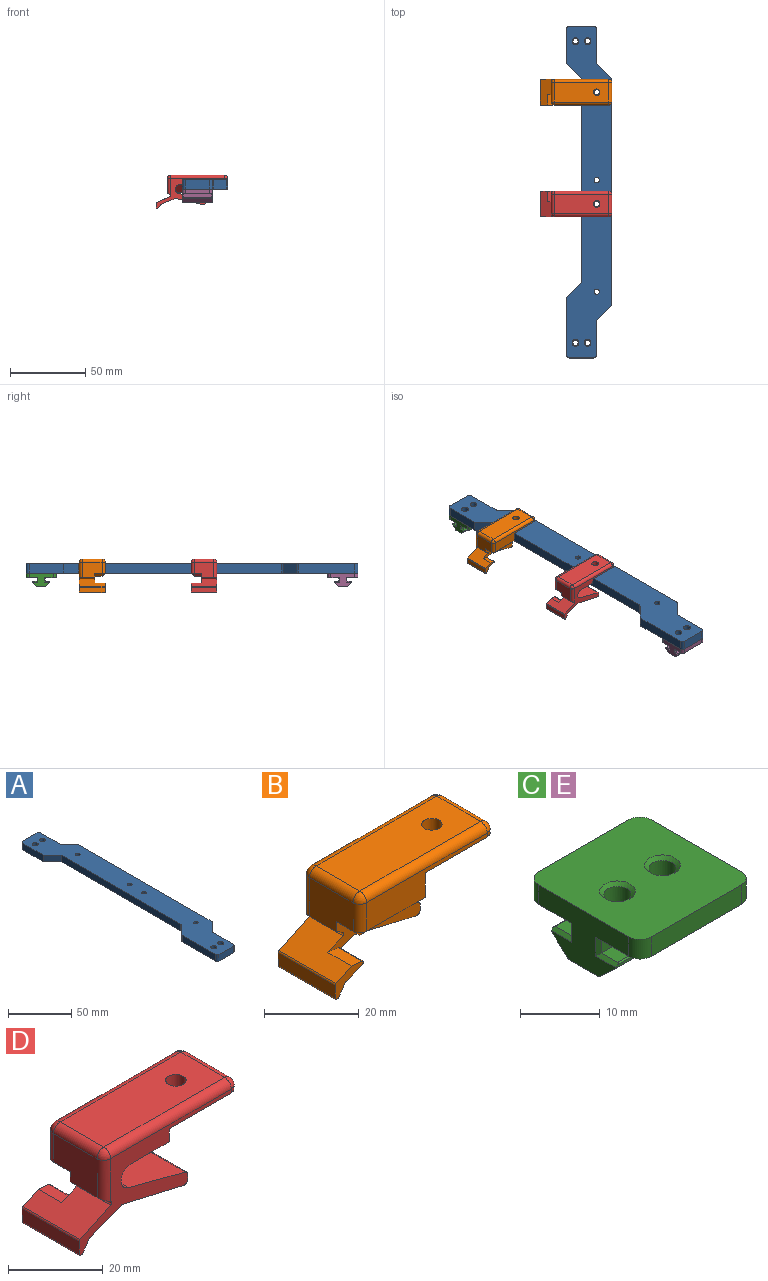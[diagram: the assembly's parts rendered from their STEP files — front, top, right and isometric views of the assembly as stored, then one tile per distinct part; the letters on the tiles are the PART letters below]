
ASSEMBLY  parts=5 mates=4
PART A: 32 faces, bbox 30x220x6.4 mm
  f0: plane 22.9x6.35mm, normal (-1,0,0), area 145.4mm2, adj f8,f9,f20,f31
  f1: plane 16x6.35mm, normal (0,-1,0), area 101.6mm2, adj f8,f9,f16,f17
  f2: plane 22.17x6.35mm, normal (1,0,0), area 140.8mm2, adj f8,f9,f16,f21
  f3: plane 148.34x6.35mm, normal (1,0,0), area 942mm2, adj f8,f9,f13,f14
  f4: plane 22.17x6.35mm, normal (1,0,0), area 140.8mm2, adj f8,f9,f18,f19
  f5: plane 16x6.35mm, normal (0,1,0), area 101.6mm2, adj f8,f9,f19,f20
  f6: plane 134.27x6.35mm, normal (-1,0,0), area 852.6mm2, adj f8,f9,f15,f31
  f7: plane 37.17x6.35mm, normal (-1,0,0), area 236mm2, adj f8,f9,f17,f22
  f8: plane 220x30mm, normal (0,0,1), area 4443.5mm2, adj f0,f1,f2,f3,f4,f5,f6,f7
  f9: plane 220x30mm, normal (0,0,-1), area 4443.5mm2, adj f0,f1,f2,f3,f4,f5,f6,f7
  f10: plane 8.83x8.83mm, normal (-0.71,0.71,0), area 79.3mm2, adj f8,f9,f15,f22
  f11: plane 8.83x8.83mm, normal (0.71,-0.71,0), area 79.3mm2, adj f8,f9,f13,f21
  f12: plane 8.83x8.83mm, normal (0.71,0.71,0), area 79.3mm2, adj f8,f9,f14,f18
  f13: cylinder r=2mm len=6.35mm, axis (0,0,1), area 10mm2, adj f3,f8,f9,f11
  f14: cylinder r=2mm len=6.35mm, axis (0,0,1), area 10mm2, adj f3,f8,f9,f12
  f15: cylinder r=2mm len=6.35mm, axis (0,0,1), area 10mm2, adj f6,f8,f9,f10
  f16: cylinder r=2mm len=6.35mm, axis (0,0,1), area 19.9mm2, adj f1,f2,f8,f9
  f17: cylinder r=2mm len=6.35mm, axis (0,0,-1), area 19.9mm2, adj f1,f7,f8,f9
  f18: cylinder r=2mm len=6.35mm, axis (0,0,1), area 10mm2, adj f4,f8,f9,f12
  f19: cylinder r=2mm len=6.35mm, axis (0,0,-1), area 19.9mm2, adj f4,f5,f8,f9
  f20: cylinder r=2mm len=6.35mm, axis (0,0,1), area 19.9mm2, adj f0,f5,f8,f9
  f21: cylinder r=2mm len=6.35mm, axis (0,0,-1), area 10mm2, adj f2,f8,f9,f11
  f22: cylinder r=2mm len=6.35mm, axis (0,0,1), area 10mm2, adj f7,f8,f9,f10
  f23: cylinder r=2.25mm len=6.35mm, axis (0,0,1), area 89.8mm2, adj f8,f9
  f24: cylinder r=2.25mm len=6.35mm, axis (0,0,1), area 89.8mm2, adj f8,f9
  f25: cylinder r=2.25mm len=6.35mm, axis (0,0,1), area 89.8mm2, adj f8,f9
  f26: cylinder r=2.25mm len=6.35mm, axis (0,0,1), area 89.8mm2, adj f8,f9
  f27: cylinder r=1.75mm len=6.35mm, axis (0,0,1), area 69.8mm2, adj f8,f9
  f28: cylinder r=1.75mm len=6.35mm, axis (0,0,1), area 69.8mm2, adj f8,f9
  f29: cylinder r=1.75mm len=6.35mm, axis (0,0,1), area 69.8mm2, adj f8,f9
  f30: cylinder r=1.75mm len=6.35mm, axis (0,0,1), area 69.8mm2, adj f8,f9
  f31: plane 10x10mm, normal (-0.71,-0.71,0), area 89.8mm2, adj f0,f6,f8,f9
PART B: 50 faces, bbox 47.4x17x22.5 mm
  f0: cylinder r=3mm len=10mm, axis (0,-1,0), area 37mm2, adj f1,f2,f8,f14,f49
  f1: cylinder r=3mm len=7.97mm, axis (0,1,0), area 28.5mm2, adj f0,f9,f14,f49
  f2: plane 27.5x10.44mm, normal (0,-1,0), area 96.4mm2, adj f0,f3,f4,f5,f6,f7,f8,f30
  f3: plane 15.5x5mm, normal (0,0,-1), area 77.5mm2, adj f2,f45,f46,f48,f49
  f4: plane 13x10mm, normal (-1,0,0), area 116.8mm2, adj f2,f5,f16,f20,f43,f45
  f5: plane 10x2.02mm, normal (-0.47,0,-0.88), area 21.9mm2, adj f2,f4,f14,f16,f37
  f6: plane 18.32x10mm, normal (-0.23,0,-0.97), area 188mm2, adj f2,f14,f36,f41
  f7: plane 10x1.26mm, normal (1,0,0), area 12.6mm2, adj f2,f14,f41,f42
  f8: plane 16.82x10mm, normal (0.25,0,0.97), area 173.8mm2, adj f0,f2,f14,f42
  f9: plane 11.31x5mm, normal (0,0,-1), area 56.6mm2, adj f1,f10,f14,f49
  f10: plane 17x6.35mm, normal (1,0,0), area 88.5mm2, adj f9,f11,f14,f15,f46,f49
  f11: plane 20.5x17mm, normal (0,0,-1), area 332.3mm2, adj f10,f12,f14,f15,f18,f25,f26
  f12: plane 13x1mm, normal (1,0,0), area 13mm2, adj f11,f18,f22,f25
  f13: plane 36x13mm, normal (0,0,1), area 453.5mm2, adj f19,f20,f22,f23,f26
  f14: plane 45.37x20.48mm, normal (0,1,0), area 226.8mm2, adj f0,f1,f5,f6,f7,f8,f9,f10
  f15: plane 36x7.35mm, normal (0,-1,0), area 147.1mm2, adj f10,f11,f23,f25,f43,f48
  f16: cylinder r=2mm len=11.07mm, axis (0,0,-1), area 32.6mm2, adj f4,f5,f14,f17
  f17: sphere r=2mm, area 6.3mm2, adj f16,f19,f20
  f18: cylinder r=2mm len=2mm, axis (0,0,1), area 3.1mm2, adj f11,f12,f14,f21
  f19: cylinder r=2mm len=36mm, axis (-1,0,0), area 113.1mm2, adj f13,f14,f17,f21
  f20: cylinder r=2mm len=13mm, axis (0,1,0), area 40.8mm2, adj f4,f13,f17,f44
  f21: sphere r=2mm, area 6.3mm2, adj f18,f19,f22
  f22: cylinder r=2mm len=13mm, axis (0,-1,0), area 40.8mm2, adj f12,f13,f21,f24
  f23: cylinder r=2mm len=36mm, axis (-1,0,0), area 113.1mm2, adj f13,f15,f24,f44
  f24: sphere r=2mm, area 6.3mm2, adj f22,f23,f25
  f25: cylinder r=2mm len=2mm, axis (0,0,1), area 3.1mm2, adj f11,f12,f15,f24
  f26: cylinder r=2.15mm len=4.3mm, axis (0,0,1), area 40.5mm2, adj f11,f13
  f27: plane 17x3.29mm, normal (-1,0,0), area 55.9mm2, adj f14,f32,f33,f38
  f28: plane 17x0.23mm, normal (0,0,-1), area 4mm2, adj f14,f33,f34,f38
  f29: plane 17x2.84mm, normal (0.83,0,-0.56), area 58.4mm2, adj f14,f34,f35,f38
  f30: plane 17x9.08mm, normal (-0.43,0,0.9), area 135.8mm2, adj f2,f14,f32,f37,f38,f39
  f31: plane 17x9.23mm, normal (0.37,0,-0.93), area 135.5mm2, adj f2,f14,f35,f36,f38,f40
  f32: cylinder r=0.5mm len=17mm, axis (0,1,0), area 9.6mm2, adj f14,f27,f30,f38
  f33: cylinder r=0.5mm len=17mm, axis (0,1,0), area 13.4mm2, adj f14,f27,f28,f38
  f34: cylinder r=0.5mm len=17mm, axis (0,1,0), area 8.3mm2, adj f14,f28,f29,f38
  f35: cylinder r=0.5mm len=17mm, axis (0,-1,0), area 5.1mm2, adj f14,f29,f31,f38
  f36: cylinder r=0.5mm len=10mm, axis (0,-1,0), area 3.1mm2, adj f2,f6,f14,f31
  f37: cylinder r=0.5mm len=10mm, axis (0,-1,0), area 11.1mm2, adj f2,f5,f14,f30
  f38: plane 8.39x6.39mm, normal (0,-1,0), area 21.8mm2, adj f27,f28,f29,f30,f31,f32,f33,f34
  f39: plane 7x3.07mm, normal (0.09,0,1), area 21.6mm2, adj f2,f30,f38,f40
  f40: cylinder r=0.5mm len=7mm, axis (0,1,0), area 9.4mm2, adj f2,f31,f38,f39
  f41: cylinder r=1mm len=10mm, axis (0,1,0), area 18mm2, adj f2,f6,f7,f14
  f42: cylinder r=1mm len=10mm, axis (0,1,0), area 13.2mm2, adj f2,f7,f8,f14
  f43: cylinder r=2mm len=7.35mm, axis (0,0,1), area 23.1mm2, adj f4,f15,f44,f47
  f44: sphere r=2mm, area 6.3mm2, adj f20,f23,f43
  f45: plane 5x2mm, normal (-0.71,0,-0.71), area 14.1mm2, adj f2,f3,f4,f47
  f46: plane 9x2mm, normal (0.71,0,-0.71), area 19.8mm2, adj f3,f10,f48,f49
  f47: cone r=2mm half-angle=45deg, axis (0,0,1), area 4.4mm2, adj f43,f45,f48
  f48: plane 17.5x2mm, normal (0,-0.71,-0.71), area 46.7mm2, adj f3,f15,f46,f47
  f49: plane 14.31x5mm, normal (0,0.71,-0.71), area 94.9mm2, adj f0,f1,f3,f9,f10,f46
PART C: 38 faces, bbox 20x20x8.8 mm
  f0: plane 20x7.85mm, normal (0,0,-1), area 145.5mm2, adj f1,f13,f14,f15,f24,f26,f28,f31
  f1: plane 19x2.4mm, normal (0,-1,0), area 45.6mm2, adj f0,f2,f28,f31
  f2: plane 19x2.9mm, normal (0,0,1), area 55.1mm2, adj f1,f16,f35,f36
  f3: plane 20x0.31mm, normal (0,-1,0), area 6.2mm2, adj f14,f15,f16,f17,f35,f36
  f4: plane 20x2.88mm, normal (0,-0.68,-0.73), area 78.8mm2, adj f14,f15,f17,f18
  f5: plane 20x5.34mm, normal (0,0,-1), area 87.6mm2, adj f14,f15,f18,f19,f22,f23
  f6: plane 20x2.88mm, normal (0,0.68,-0.73), area 78.8mm2, adj f14,f15,f19,f20
  f7: plane 20x0.31mm, normal (0,1,0), area 6.2mm2, adj f14,f15,f20,f21,f34,f37
  f8: plane 19x2.9mm, normal (0,0,1), area 55.1mm2, adj f9,f21,f34,f37
  f9: plane 19x2.4mm, normal (0,1,0), area 45.6mm2, adj f8,f10,f29,f30
  f10: plane 20x7.85mm, normal (0,0,-1), area 145.5mm2, adj f9,f11,f14,f15,f25,f27,f29,f30
  f11: plane 16x3mm, normal (0,1,0), area 48mm2, adj f10,f12,f25,f27
  f12: plane 20x20mm, normal (0,0,1), area 364.8mm2, adj f11,f13,f14,f15,f24,f25,f26,f27
  f13: plane 16x3mm, normal (0,-1,0), area 48mm2, adj f0,f12,f24,f26
  f14: plane 16x8.8mm, normal (1,0,0), area 85.4mm2, adj f0,f3,f4,f5,f6,f7,f10,f12
  f15: plane 16x8.8mm, normal (-1,0,0), area 85.4mm2, adj f0,f3,f4,f5,f6,f7,f10,f12
  f16: cylinder r=0.2mm len=19.4mm, axis (-1,0,0), area 6mm2, adj f2,f3,f35,f36
  f17: cylinder r=0.2mm len=20mm, axis (-1,0,0), area 3.3mm2, adj f3,f4,f14,f15
  f18: cylinder r=0.2mm len=20mm, axis (-1,0,0), area 3mm2, adj f4,f5,f14,f15
  f19: cylinder r=0.2mm len=20mm, axis (-1,0,0), area 3mm2, adj f5,f6,f14,f15
  f20: cylinder r=0.2mm len=20mm, axis (-1,0,0), area 3.3mm2, adj f6,f7,f14,f15
  f21: cylinder r=0.2mm len=19.4mm, axis (-1,0,0), area 6mm2, adj f7,f8,f34,f37
  f22: cylinder r=1.75mm len=8.3mm, axis (0,0,1), area 91.3mm2, adj f5,f33
  f23: cylinder r=1.75mm len=8.3mm, axis (0,0,1), area 91.3mm2, adj f5,f32
  f24: cylinder r=2mm len=3mm, axis (0,0,-1), area 9.4mm2, adj f0,f12,f13,f15
  f25: cylinder r=2mm len=3mm, axis (0,0,1), area 9.4mm2, adj f10,f11,f12,f15
  f26: cylinder r=2mm len=3mm, axis (0,0,1), area 9.4mm2, adj f0,f12,f13,f14
  f27: cylinder r=2mm len=3mm, axis (0,0,-1), area 9.4mm2, adj f10,f11,f12,f14
  f28: plane 2.9x0.5mm, normal (-0.71,-0.71,0), area 1.9mm2, adj f0,f1,f15,f35
  f29: plane 2.9x0.5mm, normal (-0.71,0.71,0), area 1.9mm2, adj f9,f10,f15,f34
  f30: plane 2.9x0.5mm, normal (0.71,0.71,0), area 1.9mm2, adj f9,f10,f14,f37
  f31: plane 2.9x0.5mm, normal (0.71,-0.71,0), area 1.9mm2, adj f0,f1,f14,f36
  f32: cone r=1.75mm half-angle=45deg, axis (0,0,1), area 8.9mm2, adj f12,f23
  f33: cone r=1.75mm half-angle=45deg, axis (0,0,1), area 8.9mm2, adj f12,f22
  f34: plane 3.6x0.5mm, normal (-0.71,0,0.71), area 2.4mm2, adj f7,f8,f15,f21,f29
  f35: plane 3.6x0.5mm, normal (-0.71,0,0.71), area 2.4mm2, adj f2,f3,f15,f16,f28
  f36: plane 3.6x0.5mm, normal (0.71,0,0.71), area 2.4mm2, adj f2,f3,f14,f16,f31
  f37: plane 3.6x0.5mm, normal (0.71,0,0.71), area 2.4mm2, adj f7,f8,f14,f21,f30
PART D: 50 faces, bbox 47.4x17x22.5 mm
  f0: cylinder r=3mm len=7.97mm, axis (0,-1,0), area 28.5mm2, adj f1,f9,f14,f49
  f1: cylinder r=3mm len=10mm, axis (0,1,0), area 37mm2, adj f0,f2,f8,f14,f49
  f2: plane 27.5x10.44mm, normal (0,1,0), area 96.4mm2, adj f1,f3,f4,f5,f6,f7,f8,f30
  f3: plane 15.5x5mm, normal (0,0,-1), area 77.5mm2, adj f2,f45,f46,f48,f49
  f4: plane 13x10mm, normal (-1,0,0), area 116.7mm2, adj f2,f5,f16,f20,f43,f45
  f5: plane 10x2.02mm, normal (-0.47,0,-0.88), area 21.9mm2, adj f2,f4,f14,f16,f37
  f6: plane 18.32x10mm, normal (-0.23,0,-0.97), area 188mm2, adj f2,f14,f36,f41
  f7: plane 10x1.26mm, normal (1,0,0), area 12.6mm2, adj f2,f14,f41,f42
  f8: plane 16.82x10mm, normal (0.25,0,0.97), area 173.8mm2, adj f1,f2,f14,f42
  f9: plane 11.31x5mm, normal (0,0,-1), area 56.6mm2, adj f0,f10,f14,f49
  f10: plane 17x6.35mm, normal (1,0,0), area 88.4mm2, adj f9,f11,f14,f15,f46,f49
  f11: plane 20.5x17mm, normal (0,0,-1), area 332.3mm2, adj f10,f12,f14,f15,f18,f25,f26
  f12: plane 13x1mm, normal (1,0,0), area 13mm2, adj f11,f18,f22,f25
  f13: plane 36x13mm, normal (0,0,1), area 453.5mm2, adj f19,f20,f22,f23,f26
  f14: plane 45.37x20.48mm, normal (0,-1,0), area 226.8mm2, adj f0,f1,f5,f6,f7,f8,f9,f10
  f15: plane 36x7.35mm, normal (0,1,0), area 147.1mm2, adj f10,f11,f23,f25,f43,f48
  f16: cylinder r=2mm len=11.07mm, axis (0,0,-1), area 32.6mm2, adj f4,f5,f14,f17
  f17: sphere r=2mm, area 6.3mm2, adj f16,f19,f20
  f18: cylinder r=2mm len=2mm, axis (0,0,1), area 3.1mm2, adj f11,f12,f14,f21
  f19: cylinder r=2mm len=36mm, axis (-1,0,0), area 113.1mm2, adj f13,f14,f17,f21
  f20: cylinder r=2mm len=13mm, axis (0,-1,0), area 40.8mm2, adj f4,f13,f17,f44
  f21: sphere r=2mm, area 6.3mm2, adj f18,f19,f22
  f22: cylinder r=2mm len=13mm, axis (0,1,0), area 40.8mm2, adj f12,f13,f21,f24
  f23: cylinder r=2mm len=36mm, axis (-1,0,0), area 113.1mm2, adj f13,f15,f24,f44
  f24: sphere r=2mm, area 6.3mm2, adj f22,f23,f25
  f25: cylinder r=2mm len=2mm, axis (0,0,1), area 3.1mm2, adj f11,f12,f15,f24
  f26: cylinder r=2.15mm len=4.3mm, axis (0,0,1), area 40.5mm2, adj f11,f13
  f27: plane 17x3.29mm, normal (-1,0,0), area 55.9mm2, adj f14,f32,f33,f38
  f28: plane 17x0.23mm, normal (0,0,-1), area 4mm2, adj f14,f33,f34,f38
  f29: plane 17x2.84mm, normal (0.83,0,-0.56), area 58.4mm2, adj f14,f34,f35,f38
  f30: plane 17x9.08mm, normal (-0.43,0,0.9), area 135.8mm2, adj f2,f14,f32,f37,f38,f39
  f31: plane 17x9.23mm, normal (0.37,0,-0.93), area 135.5mm2, adj f2,f14,f35,f36,f38,f40
  f32: cylinder r=0.5mm len=17mm, axis (0,-1,0), area 9.6mm2, adj f14,f27,f30,f38
  f33: cylinder r=0.5mm len=17mm, axis (0,-1,0), area 13.4mm2, adj f14,f27,f28,f38
  f34: cylinder r=0.5mm len=17mm, axis (0,-1,0), area 8.3mm2, adj f14,f28,f29,f38
  f35: cylinder r=0.5mm len=17mm, axis (0,1,0), area 5.1mm2, adj f14,f29,f31,f38
  f36: cylinder r=0.5mm len=10mm, axis (0,1,0), area 3.1mm2, adj f2,f6,f14,f31
  f37: cylinder r=0.5mm len=10mm, axis (0,1,0), area 11.1mm2, adj f2,f5,f14,f30
  f38: plane 8.39x6.39mm, normal (0,1,0), area 21.8mm2, adj f27,f28,f29,f30,f31,f32,f33,f34
  f39: plane 7x3.07mm, normal (0.09,0,1), area 21.6mm2, adj f2,f30,f38,f40
  f40: cylinder r=0.5mm len=7mm, axis (0,-1,0), area 9.4mm2, adj f2,f31,f38,f39
  f41: cylinder r=1mm len=10mm, axis (0,-1,0), area 18mm2, adj f2,f6,f7,f14
  f42: cylinder r=1mm len=10mm, axis (0,-1,0), area 13.2mm2, adj f2,f7,f8,f14
  f43: cylinder r=2mm len=7.35mm, axis (0,0,-1), area 23.1mm2, adj f4,f15,f44,f47
  f44: sphere r=2mm, area 6.3mm2, adj f20,f23,f43
  f45: plane 5x2mm, normal (-0.71,0,-0.71), area 14.1mm2, adj f2,f3,f4,f47
  f46: plane 9x2mm, normal (0.71,0,-0.71), area 19.8mm2, adj f3,f10,f48,f49
  f47: cone r=2mm half-angle=45deg, axis (0,0,1), area 4.4mm2, adj f43,f45,f48
  f48: plane 17.5x2mm, normal (0,0.71,-0.71), area 46.7mm2, adj f3,f15,f46,f47
  f49: plane 14.31x5mm, normal (0,-0.71,-0.71), area 94.9mm2, adj f0,f1,f3,f9,f10,f46
PART E: same geometry as C
PLACE A t=(3.46,-65.07,32.74)mm
PLACE B t=(3.46,-65.07,32.74)mm
PLACE C t=(3.46,134.93,32.74)mm
PLACE D t=(3.46,-65.07,32.74)mm
PLACE E t=(3.46,-65.07,32.74)mm
MATE fastened A.f23 <-> C.f32  axis (0,0,-1) through (17.46,134.93,34.24)mm
MATE fastened B.f26 <-> A.f27  axis (0,0,-1) through (23.46,101.03,40.59)mm
MATE fastened A.f25 <-> E.f32  axis (0,0,-1) through (17.46,-65.07,34.24)mm
MATE fastened D.f26 <-> A.f28  axis (0,0,-1) through (23.46,27.03,40.59)mm
